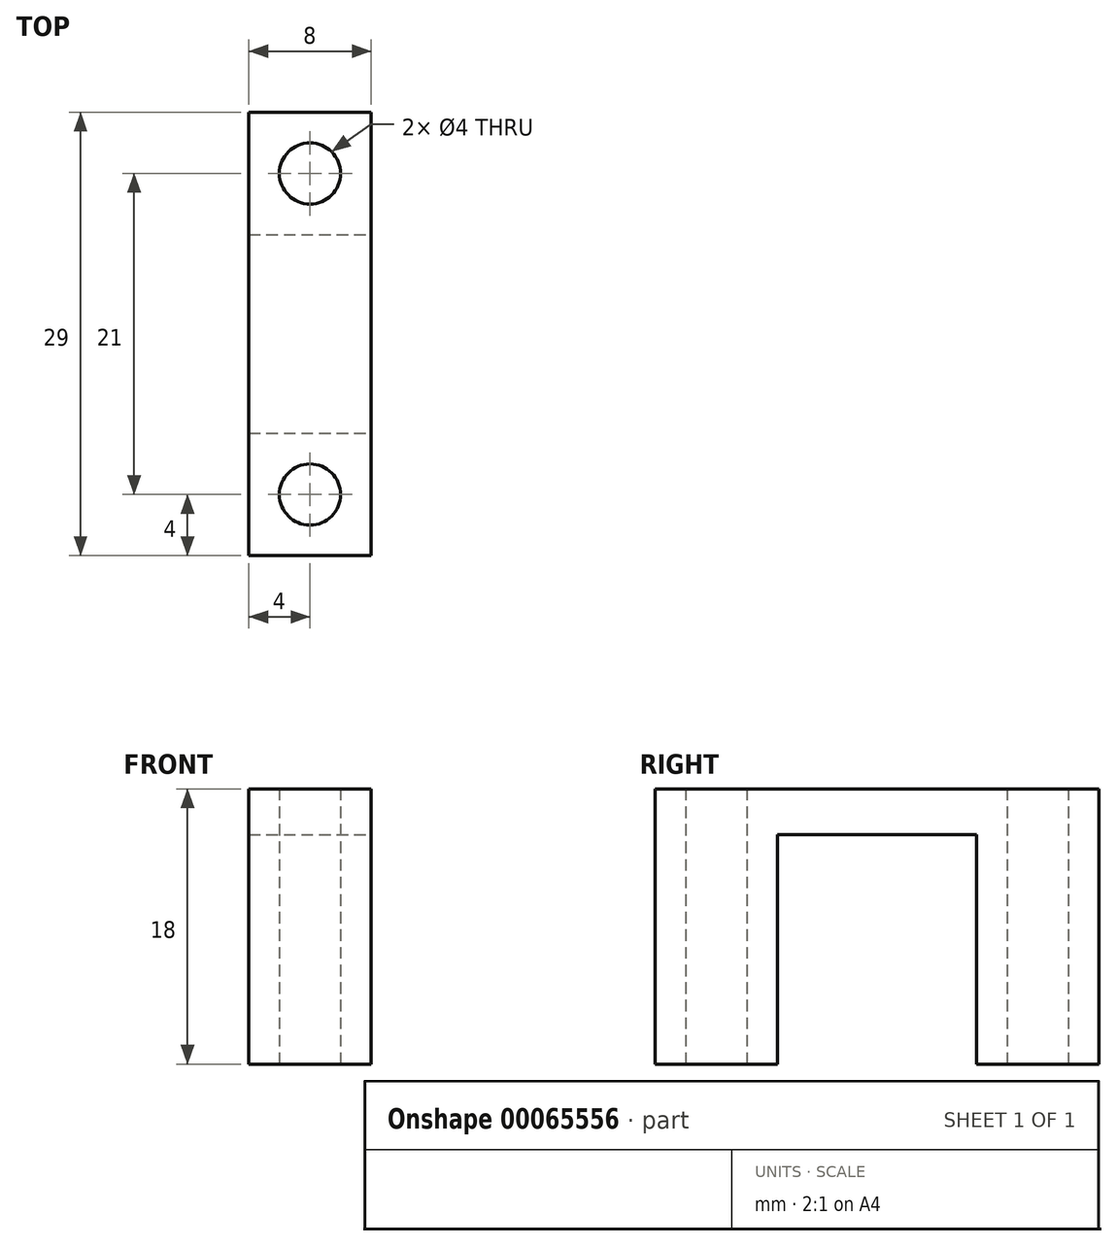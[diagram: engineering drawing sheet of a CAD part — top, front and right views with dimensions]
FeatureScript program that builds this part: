
annotation { "Feature Type Name" : "Feature", "Feature Type Description" : "" }
export const myFeature = defineFeature(function(context is Context, id is Id, definition is map)
    precondition{}
    {
        {
            var Q0;
            Q0=qCreatedBy(makeId("Top.planeOp"),FACE);
            var sketch = newSketch(context, id + "F0", { "sketchPlane" : qUnion([Q0])});
            skLineSegment(sketch, "E0.bottom", {"start": v(-4, 14.5) * mm, "end": v(4, 14.5) * mm});
            skLineSegment(sketch, "E0.top", {"start": v(-4, 6.5) * mm, "end": v(4, 6.5) * mm});
            skLineSegment(sketch, "E0.left", {"start": v(-4, 14.5) * mm, "end": v(-4, 6.5) * mm});
            skLineSegment(sketch, "E0.right", {"start": v(4, 14.5) * mm, "end": v(4, 6.5) * mm});
            skCircle(sketch, "E1", {"center": v(0, 10.5) * mm, "radius": 2 * mm});
            skPoint(sketch, "E1.centerSnap0", {"position": v(4, 10.5) * mm});
            skPoint(sketch, "E1.centerSnap1", {"position": v(0, 14.5) * mm});
            skLineSegment(sketch, "E2.top", {"start": v(-4, -14.5) * mm, "end": v(4, -14.5) * mm});
            skLineSegment(sketch, "E2.left", {"start": v(-4, -6.5) * mm, "end": v(-4, -14.5) * mm});
            skLineSegment(sketch, "E2.right", {"start": v(4, -6.5) * mm, "end": v(4, -14.5) * mm});
            skCircle(sketch, "E3", {"center": v(0, -10.5) * mm, "radius": 2 * mm});
            skLineSegment(sketch, "E2.bottom", {"start": v(-4, -6.5) * mm, "end": v(4, -6.5) * mm});
            skPoint(sketch, "E3.centerSnap0", {"position": v(4, -10.5) * mm});
            skPoint(sketch, "E3.centerSnap1", {"position": v(0, -6.5) * mm});
            skLineSegment(sketch, "E4", {"start": v(-4, 6.5) * mm, "end": v(-4, -6.5) * mm});
            skLineSegment(sketch, "E5", {"start": v(4, 6.5) * mm, "end": v(4, -6.5) * mm});
            skLineSegment(sketch, "E6", {"start": v(4, 0) * mm, "end": v(-4, 0) * mm, "construction": true});
            skSolve(sketch);
        }
        {
            var Q0;
            Q0=makeQuery(id+"F0.imprint","IMPRINT",FACE,{"disambiguationData":[TD([[makeQuery(id+"F0.imprint","IMPRINT",EDGE,{"derivedFrom":sQuery(id+"F0.wireOp",EDGE,"E0.bottom")}),-1.0]])]});
            var Q1;
            Q1=makeQuery(id+"F0.imprint","IMPRINT",FACE,{"disambiguationData":[TD([[makeQuery(id+"F0.imprint","IMPRINT",EDGE,{"derivedFrom":sQuery(id+"F0.wireOp",EDGE,"E0.top")}),-1.0]])]});
            var Q2;
            Q2=makeQuery(id+"F0.imprint","IMPRINT",FACE,{"disambiguationData":[TD([[makeQuery(id+"F0.imprint","IMPRINT",EDGE,{"derivedFrom":sQuery(id+"F0.wireOp",EDGE,"E2.top")}),1.0]])]});
            extrude(context, id + "F1", {"entities" : qUnion([Q0, Q1, Q2]), "depth" : 3 * mm});
        }
        {
            var Q0;
            Q0=makeQuery(id+"F0.imprint","IMPRINT",FACE,{"disambiguationData":[TD([[makeQuery(id+"F0.imprint","IMPRINT",EDGE,{"derivedFrom":sQuery(id+"F0.wireOp",EDGE,"E0.bottom")}),-1.0]])]});
            var Q1;
            Q1=makeQuery(id+"F0.imprint","IMPRINT",FACE,{"disambiguationData":[TD([[makeQuery(id+"F0.imprint","IMPRINT",EDGE,{"derivedFrom":sQuery(id+"F0.wireOp",EDGE,"E2.top")}),1.0]])]});
            extrude(context, id + "F2", {"entities" : qUnion([Q0, Q1]), "operationType" : NewBodyOperationType.ADD, "oppositeDirection" : true, "depth" : 15 * mm});
        }
    });
